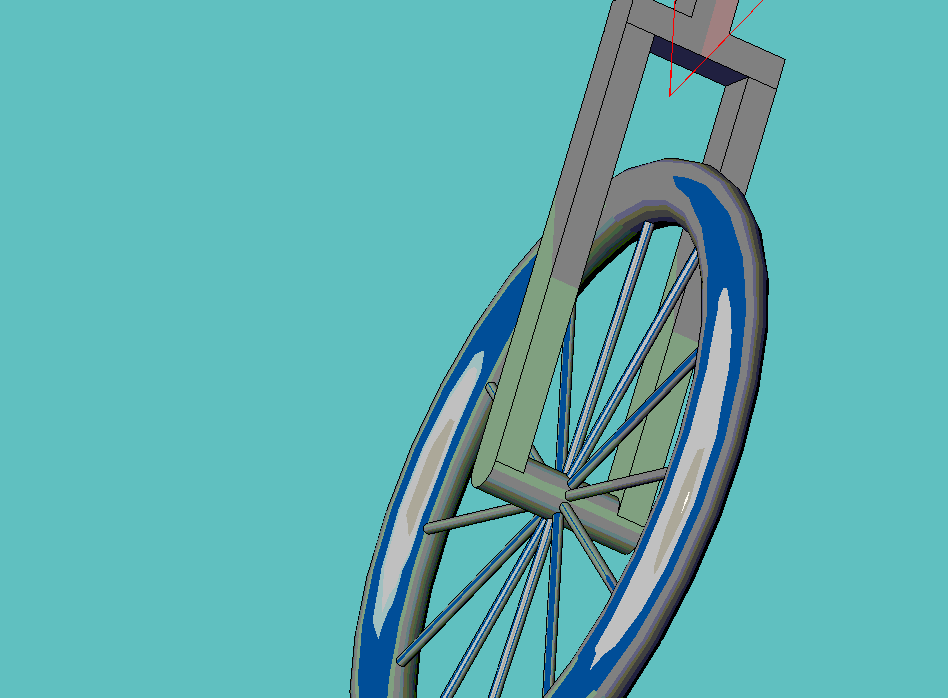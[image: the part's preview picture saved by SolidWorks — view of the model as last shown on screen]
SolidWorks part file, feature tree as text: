
SOLIDWORKS PART (.sldprt)
format: sldprt  version: not decoded by parser v0  size: 1,338,880 bytes
history: native  units: mm
features: sketch x12, extrude x7, plane x4, helix x2, sweep x2, material x1, revolve x1, pattern_circular x1, mirror x1 (+12 scaffold rows collapsed)
feature tree (43):
  scaffold x12  (default folders/planes/origin — collapsed)
  material  "Material <not specified>"
  sketch  "Sketch2"  dims[D2=3.0mm D1=15.0mm]
  revolve  "Revolve1"  Angle=360deg
  plane  "Plane1"  Offset=5mm
  sketch  "Sketch5"  dims[D1=0.5mm]
  sketch  "Sketch6"
  extrude  "Extrude1"  Depth=4mm
  extrude  "Extrude2"  [1 undecoded]
  pattern_circular  "CirPattern1"  Count=12 Angle=30deg
  sketch  "Sketch7"  dims[D1=0.0mm]
  extrude  "Extrude3"  Depth=1.5mm
  mirror  "Mirror1"
  sketch  "Sketch8"
  extrude  "Extrude4"  Depth=1.5mm
  sketch  "Sketch9"  dims[D1=3.0mm D2=3.0mm D3=2.2281mm]
  extrude  "Extrude5"  Depth=40mm
  sketch  "Sketch10"
  extrude  "Extrude6"  Depth=10mm
  plane  "Plane2"
  sketch  "Sketch11"
  extrude  "Extrude7"  [1 undecoded]
  sketch  "Sketch13"  dims[D1=~0.977365mm]
  helix  "Helix/Spiral1"  Pitch=4.25mm
  plane  "Plane3"  Offset=1mm
  sketch  "Sketch15"
  sweep  "Sweep1"
  plane  "Plane4"
  sketch  "Sketch17"
  helix  "Helix/Spiral2"  Pitch=4.25mm
  sweep  "Sweep2"
  sketch  "Sketch15<2>"
decode coverage: 14 of 26 modeling features carry decoded parameters
note: ~ marks probable driven/reference dimensions
note: 2 parameter values undecoded
note: suppression state not decoded; provenance and decode notes live in map.json
